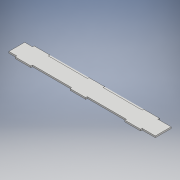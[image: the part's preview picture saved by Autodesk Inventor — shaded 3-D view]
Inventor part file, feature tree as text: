
AUTODESK INVENTOR PART (.ipt)
format: ipt  version: 2018 (Build 220112000, 112)  size: 121,344 bytes
history: native  units: mm
features: extrude x1, sketch x1
ambient origin geometry x8: Origin, YZ Plane, XZ Plane, XY Plane, X Axis, Y Axis, Z Axis, Center Point
bodies: Body1 (feature_tree)
feature tree (2):
  extrude  "Extrusion2"  Depth=4.0mm TaperAngle=0.0deg
  sketch  "Sketch1"  dims[d1=40.0mm d8=4.0mm d9=0.0mm]
